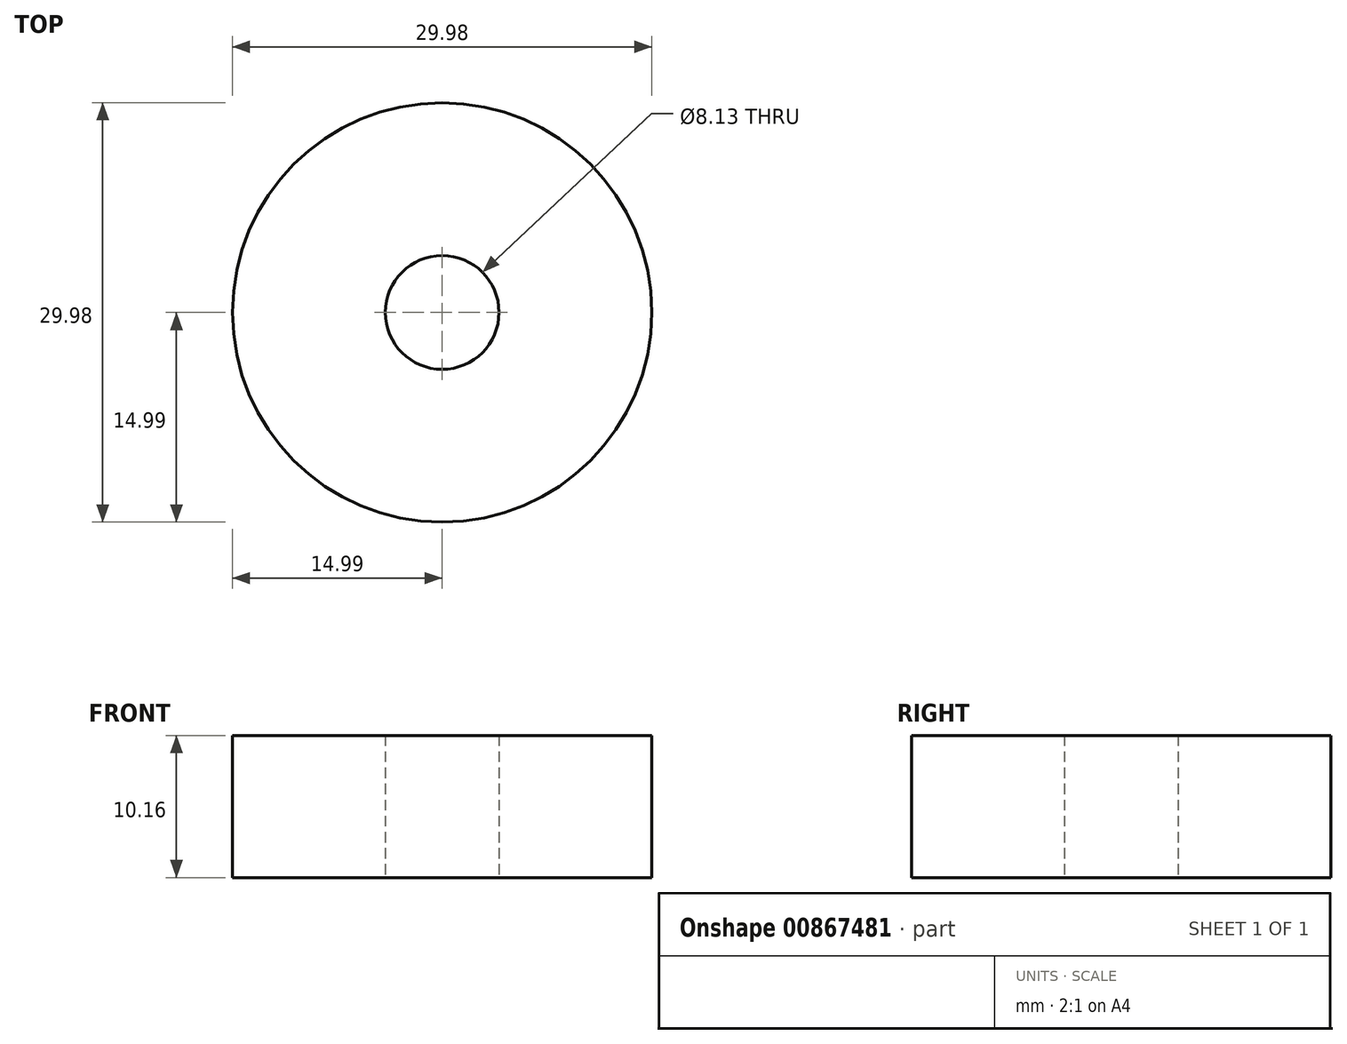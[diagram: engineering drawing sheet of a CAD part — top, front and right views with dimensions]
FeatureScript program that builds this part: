
annotation { "Feature Type Name" : "Feature", "Feature Type Description" : "" }
export const myFeature = defineFeature(function(context is Context, id is Id, definition is map)
    precondition{}
    {
        {
            var Q0;
            Q0=qCreatedBy(makeId("Top.planeOp"),FACE);
            var sketch = newSketch(context, id + "F0", { "sketchPlane" : qUnion([Q0])});
            skCircle(sketch, "E0", {"center": v(0, 0) * mm, "radius": 14.99 * mm});
            skCircle(sketch, "E1", {"center": v(0, 0) * mm, "radius": 4.06 * mm});
            skSolve(sketch);
        }
        {
            var Q0;
            Q0=makeQuery(id+"F0.imprint","IMPRINT",FACE,{"disambiguationData":[TD([[makeQuery(id+"F0.imprint","IMPRINT",EDGE,{"derivedFrom":sQuery(id+"F0.wireOp",EDGE,"E0")}),1.0]])]});
            extrude(context, id + "F1", {"entities" : qUnion([Q0]), "depth" : 10.16 * mm, "offsetDistance" : 25.4 * mm});
        }
    });
